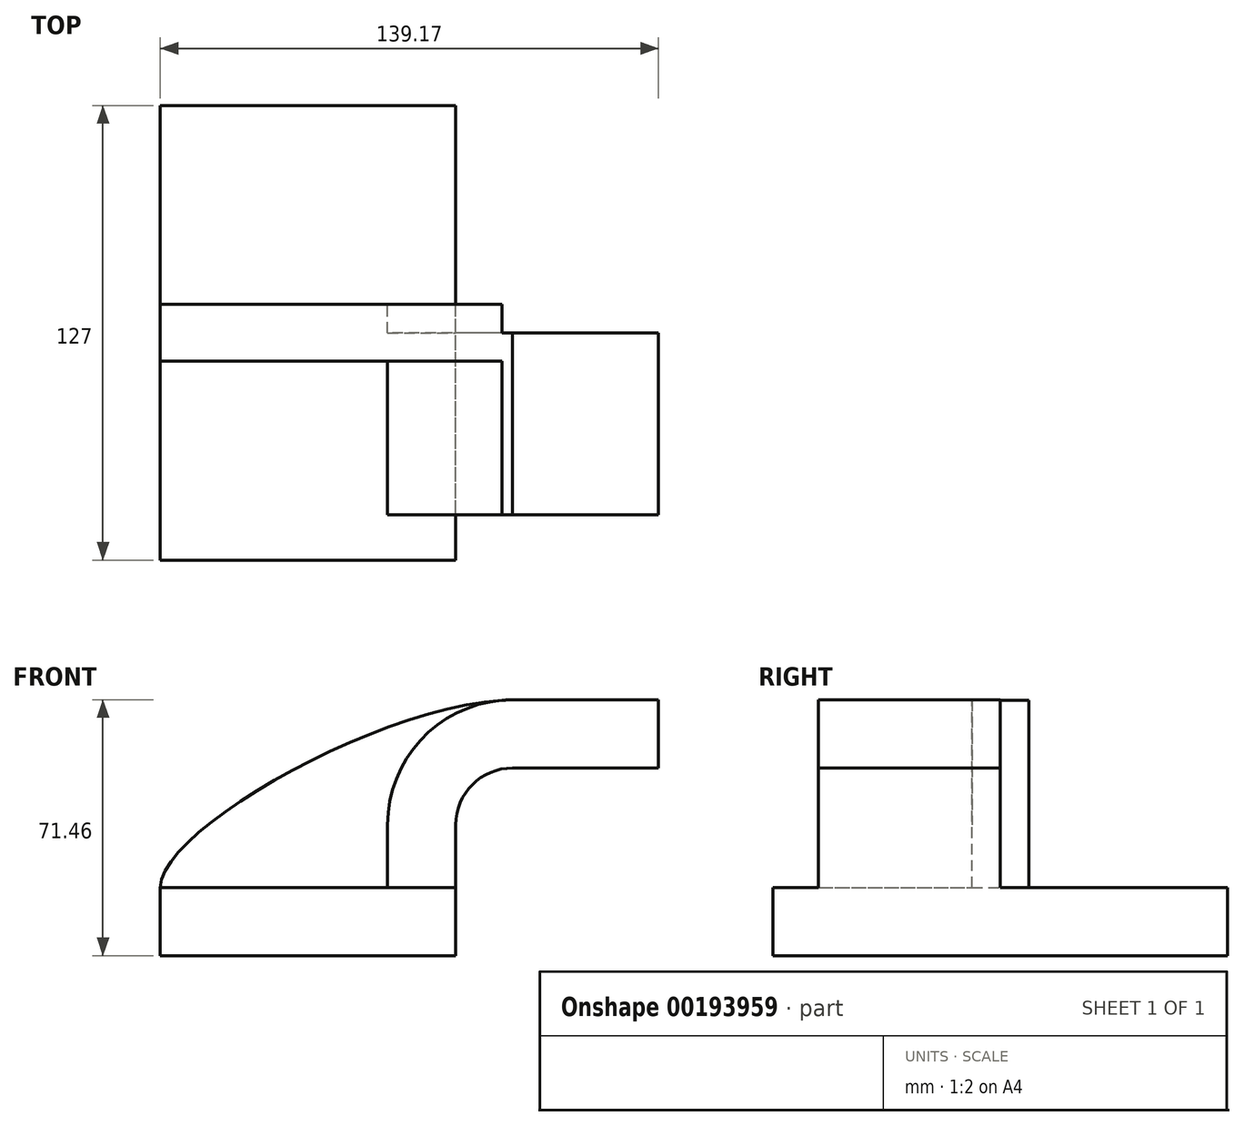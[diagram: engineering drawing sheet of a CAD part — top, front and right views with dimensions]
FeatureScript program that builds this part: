
annotation { "Feature Type Name" : "Feature", "Feature Type Description" : "" }
export const myFeature = defineFeature(function(context is Context, id is Id, definition is map)
    precondition{}
    {
        {
            var Q0;
            Q0=qCreatedBy(makeId("Front.planeOp"),FACE);
            var sketch = newSketch(context, id + "F0", { "sketchPlane" : qUnion([Q0])});
            skLineSegment(sketch, "E0.bottom", {"start": v(-41.28, -9.53) * mm, "end": v(41.28, -9.53) * mm});
            skLineSegment(sketch, "E0.top", {"start": v(-41.28, 9.52) * mm, "end": v(41.28, 9.52) * mm});
            skLineSegment(sketch, "E0.left", {"start": v(-41.27, -9.53) * mm, "end": v(-41.28, 9.52) * mm});
            skLineSegment(sketch, "E0.right", {"start": v(41.28, -9.53) * mm, "end": v(41.28, 9.52) * mm});
            skPoint(sketch, "E0.middle", {"position": v(0, 0) * mm});
            skLineSegment(sketch, "E1.bottom", {"start": v(123.3, 38.1) * mm, "end": v(72.5, 38.1) * mm});
            skLineSegment(sketch, "E1.top", {"start": v(123.3, 66.67) * mm, "end": v(72.5, 66.67) * mm});
            skLineSegment(sketch, "E1.left", {"start": v(123.3, 38.1) * mm, "end": v(123.3, 66.67) * mm});
            skLineSegment(sketch, "E1.right", {"start": v(72.5, 38.1) * mm, "end": v(72.5, 66.67) * mm});
            skPoint(sketch, "E1.middle", {"position": v(97.9, 52.39) * mm});
            skLineSegment(sketch, "E2", {"start": v(41.27, 9.52) * mm, "end": v(41.27, 27) * mm});
            skArc(sketch, "E3", {"start": v(41.27, 27) * mm, "mid": v(45.92, 38.23) * mm, "end": v(57.15, 42.88) * mm});
            skLineSegment(sketch, "E4", {"start": v(57.15, 42.88) * mm, "end": v(97.89, 42.88) * mm});
            skLineSegment(sketch, "E5.0", {"start": v(57.15, 61.93) * mm, "end": v(97.89, 61.93) * mm});
            skArc(sketch, "E5.1", {"start": v(22.22, 27) * mm, "mid": v(32.45, 51.7) * mm, "end": v(57.15, 61.93) * mm});
            skLineSegment(sketch, "E5.2", {"start": v(22.22, 9.52) * mm, "end": v(22.22, 27) * mm});
            skPoint(sketch, "E6.visualSharp", {"position": v(-41.28, 9.52) * mm});
            skLineSegment(sketch, "E6.filletArc", {"start": v(-41.28, 9.52) * mm, "end": v(-41.28, 9.52) * mm});
            skLineSegment(sketch, "E7", {"start": v(97.89, 38.1) * mm, "end": v(97.89, 66.67) * mm});
            skPoint(sketch, "E7.startSnap0", {"position": v(97.9, 38.1) * mm});
            skFitSpline(sketch, "E8", {"points": [v(-41.28, 9.52) * mm, v(57.15, 61.93) * mm], "startDerivative": vector(1, 50.07) * mm, "endDerivative": vector(106.73, 1.89) * mm});
            skPoint(sketch, "E9.1.internal.snap0", {"position": v(32.45, 51.7) * mm});
            skSolve(sketch);
        }
        {
            var Q0;
            Q0=makeQuery(id+"F0.imprint","IMPRINT",FACE,{"disambiguationData":[TD([[makeQuery(id+"F0.imprint","IMPRINT",EDGE,{"derivedFrom":sQuery(id+"F0.wireOp",EDGE,"E0.bottom")}),1.0]])]});
            extrude(context, id + "F1", {"entities" : qUnion([Q0]), "endBound" : BoundingType.SYMMETRIC, "depth" : 127 * mm});
        }
        {
            var Q0;
            {var subQ0=sQuery(id+"F0.wireOp",EDGE,"E4");var subQ1=sQuery(id+"F0.wireOp",EDGE,"E1.right");var subQ2=makeQuery(id+"F0.imprint","INTERSECT",VERTEX,{"derivedFrom":[subQ1,subQ0]});Q0=makeQuery(id+"F0.imprint","IMPRINT",FACE,{"disambiguationData":[TD([[makeQuery(id+"F0.imprint","IMPRINT",EDGE,{"disambiguationData":[TD([[subQ2,-1.0]])],"derivedFrom":subQ1}),-1.0]])]});}
            var Q1;
            {var subQ1=sQuery(id+"F0.wireOp",EDGE,"E2");Q1=makeQuery(id+"F0.imprint","IMPRINT",FACE,{"disambiguationData":[TD([[makeQuery(id+"F0.imprint","IMPRINT",EDGE,{"derivedFrom":subQ1}),1.0]])]});}
            extrude(context, id + "F2", {"entities" : qUnion([Q0, Q1]), "operationType" : NewBodyOperationType.ADD, "depth" : 50.8 * mm});
        }
        {
            var Q0;
            {var subQ3=sQuery(id+"F0.wireOp",EDGE,"E5.2");Q0=makeQuery(id+"F0.imprint","IMPRINT",FACE,{"disambiguationData":[TD([[makeQuery(id+"F0.imprint","IMPRINT",EDGE,{"derivedFrom":subQ3}),1.0]])]});}
            extrude(context, id + "F3", {"entities" : qUnion([Q0]), "operationType" : NewBodyOperationType.ADD, "endBound" : BoundingType.SYMMETRIC, "depth" : 15.88 * mm});
        }
    });
